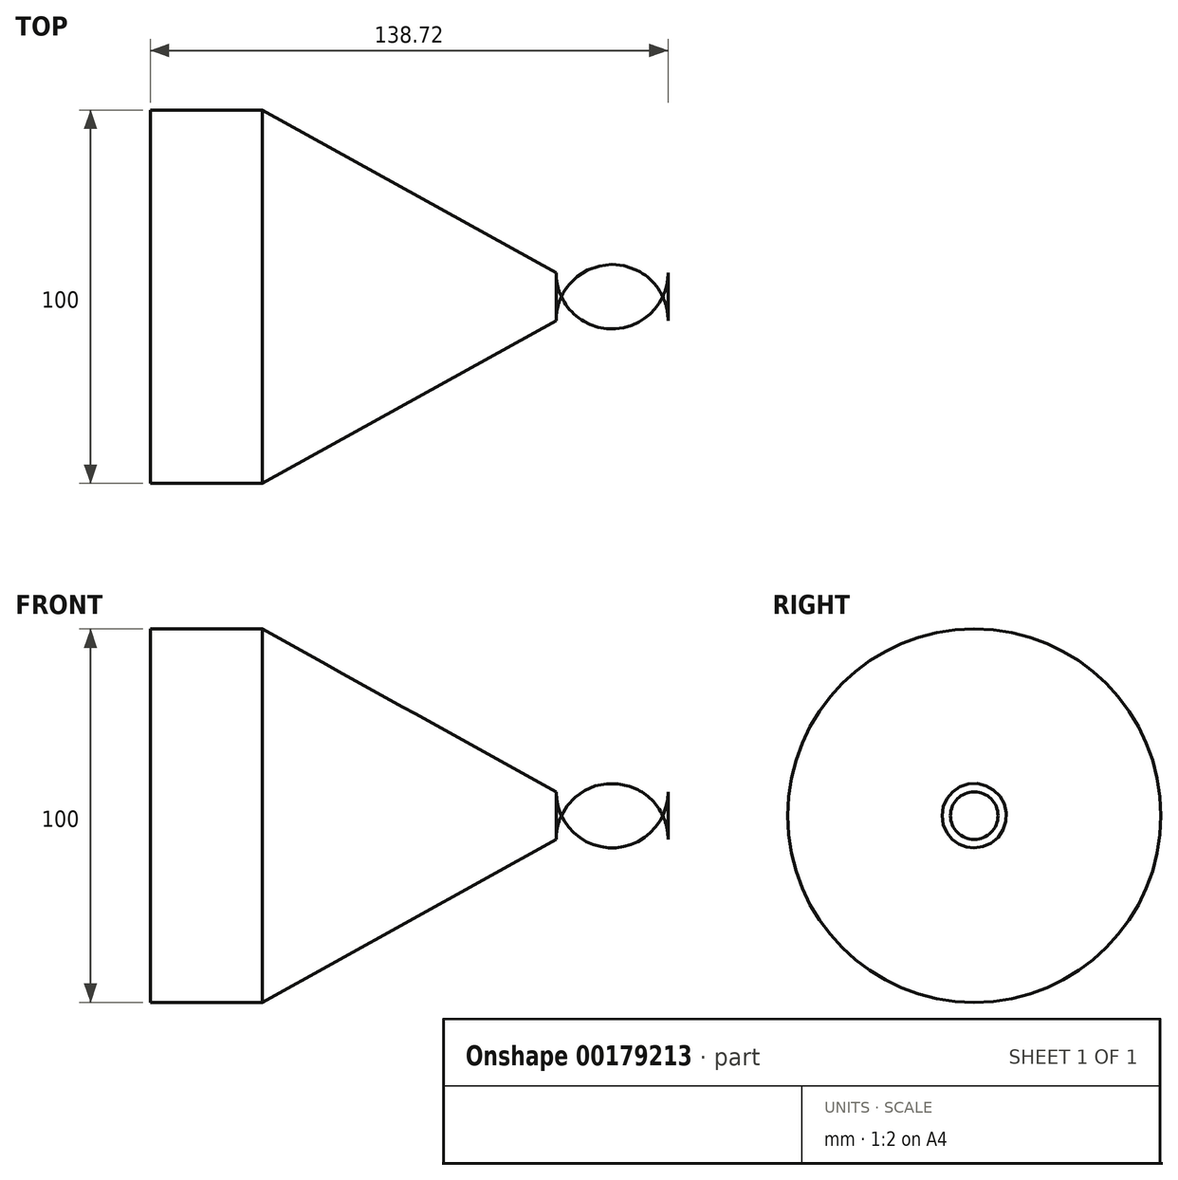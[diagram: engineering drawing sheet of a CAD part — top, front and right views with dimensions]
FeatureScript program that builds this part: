
annotation { "Feature Type Name" : "Feature", "Feature Type Description" : "" }
export const myFeature = defineFeature(function(context is Context, id is Id, definition is map)
    precondition{}
    {
        {
            var Q0;
            Q0=qCreatedBy(makeId("Front.planeOp"),FACE);
            var sketch = newSketch(context, id + "F0", { "sketchPlane" : qUnion([Q0])});
            skLineSegment(sketch, "E0", {"start": v(0, 0) * mm, "end": v(150, 0) * mm, "construction": true});
            skLineSegment(sketch, "E1", {"start": v(0, 0) * mm, "end": v(0, 50) * mm});
            skLineSegment(sketch, "E2", {"start": v(0, 50) * mm, "end": v(30, 50) * mm});
            skLineSegment(sketch, "E3", {"start": v(30, 50) * mm, "end": v(108.72, 6.37) * mm});
            skLineSegment(sketch, "E4", {"start": v(108.72, 6.37) * mm, "end": v(138.72, 6.37) * mm, "construction": true});
            skLineSegment(sketch, "E5", {"start": v(138.72, 6.37) * mm, "end": v(123.72, 6.37) * mm, "construction": true});
            skArc(sketch, "E6", {"start": v(138.72, 6.37) * mm, "mid": v(123.72, 21.37) * mm, "end": v(108.72, 6.37) * mm});
            skLineSegment(sketch, "E7", {"start": v(138.72, 6.37) * mm, "end": v(138.72, 0) * mm});
            skLineSegment(sketch, "E8", {"start": v(138.72, 0) * mm, "end": v(0, 0) * mm});
            skSolve(sketch);
        }
        {
            var Q0;
            Q0 = qSketchRegion(id + "F0", true);
            var Q1;
            Q1=sQuery(id+"F0.wireOp",EDGE,"E0");
            revolve(context, id + "F1", {"entities" : qUnion([Q0]), "axis" : qUnion([Q1]), "revolveType" : RevolveType.FULL});
        }
    });
